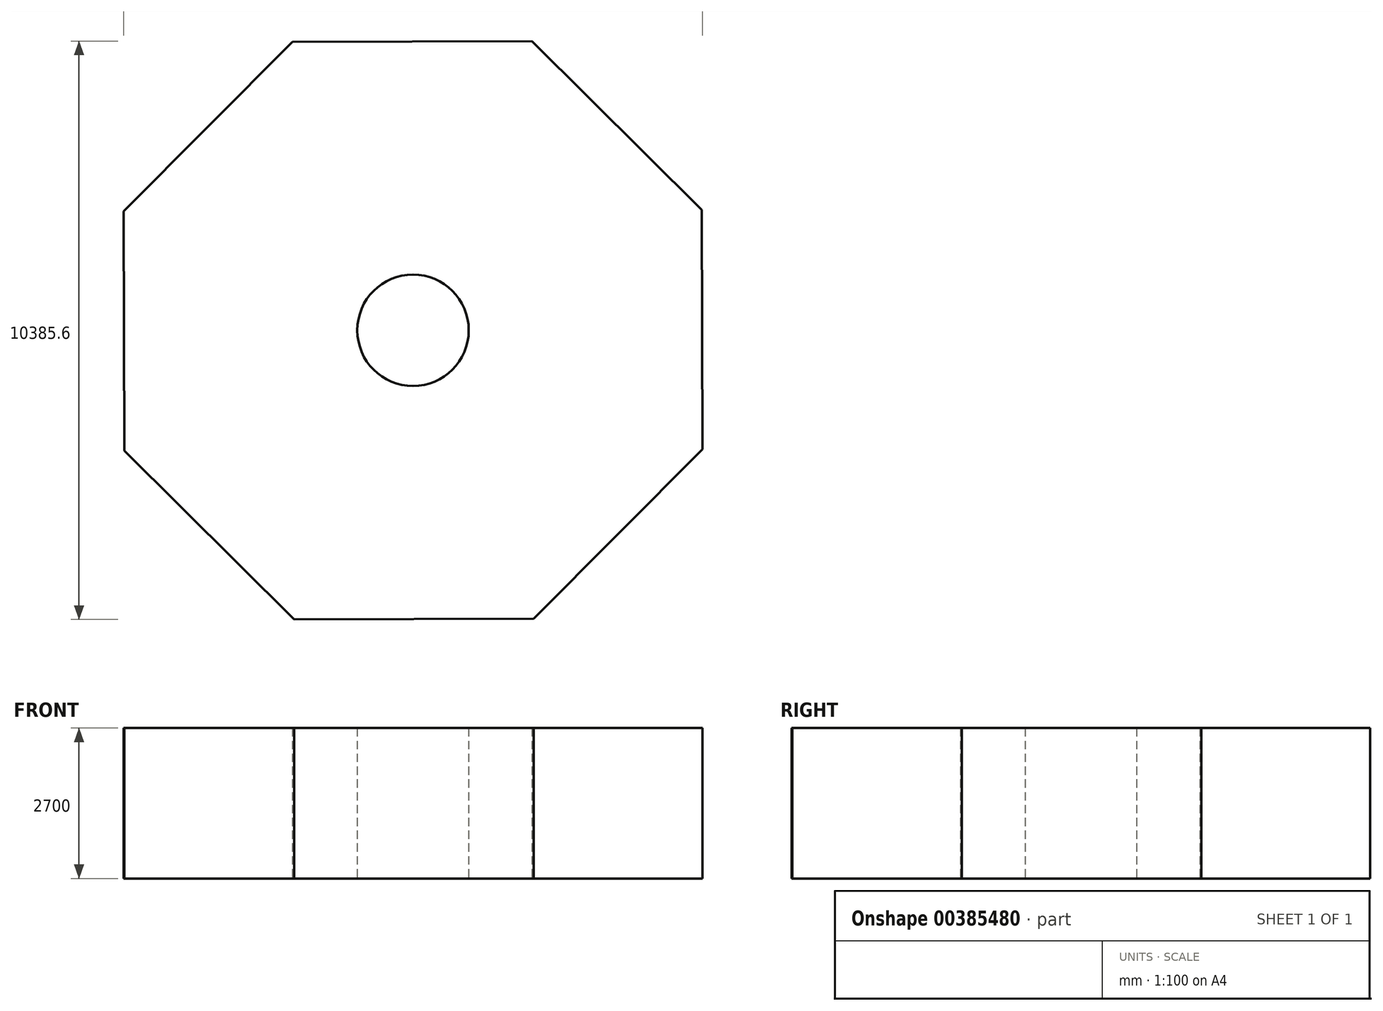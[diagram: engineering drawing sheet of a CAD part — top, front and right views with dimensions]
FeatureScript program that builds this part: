
annotation { "Feature Type Name" : "Feature", "Feature Type Description" : "" }
export const myFeature = defineFeature(function(context is Context, id is Id, definition is map)
    precondition{}
    {
        {
            var Q0;
            Q0=qCreatedBy(makeId("Top.planeOp"),FACE);
            var sketch = newSketch(context, id + "F0", { "sketchPlane" : qUnion([Q0])});
            skCircle(sketch, "E0.cCircle", {"center": v(0, 0) * mm, "radius": 5187 * mm, "construction": true});
            skLineSegment(sketch, "E0.0", {"start": v(-2134.46, -5192.8) * mm, "end": v(-5181.16, -2162.57) * mm});
            skLineSegment(sketch, "E0.1", {"start": v(-5181.16, -2162.57) * mm, "end": v(-5192.8, 2134.46) * mm});
            skLineSegment(sketch, "E0.2", {"start": v(-5192.8, 2134.46) * mm, "end": v(-2162.57, 5181.16) * mm});
            skLineSegment(sketch, "E0.3", {"start": v(-2162.57, 5181.16) * mm, "end": v(2134.46, 5192.8) * mm});
            skLineSegment(sketch, "E0.4", {"start": v(2134.46, 5192.8) * mm, "end": v(5181.16, 2162.57) * mm});
            skLineSegment(sketch, "E0.5", {"start": v(5181.16, 2162.57) * mm, "end": v(5192.8, -2134.46) * mm});
            skLineSegment(sketch, "E0.6", {"start": v(5192.8, -2134.46) * mm, "end": v(2162.57, -5181.16) * mm});
            skLineSegment(sketch, "E0.7", {"start": v(2162.57, -5181.16) * mm, "end": v(-2134.46, -5192.8) * mm});
            skPoint(sketch, "E0.0.midPoint", {"position": v(-3657.8, -3677.69) * mm});
            skCircle(sketch, "E1", {"center": v(0, 0) * mm, "radius": 1000 * mm});
            skSolve(sketch);
        }
        {
            var Q0;
            Q0=makeQuery(id+"F0.imprint","IMPRINT",FACE,{"disambiguationData":[TD([[makeQuery(id+"F0.imprint","IMPRINT",EDGE,{"derivedFrom":sQuery(id+"F0.wireOp",EDGE,"E0.0")}),-1.0]])]});
            extrude(context, id + "F1", {"entities" : qUnion([Q0]), "depth" : 2700 * mm});
        }
    });
